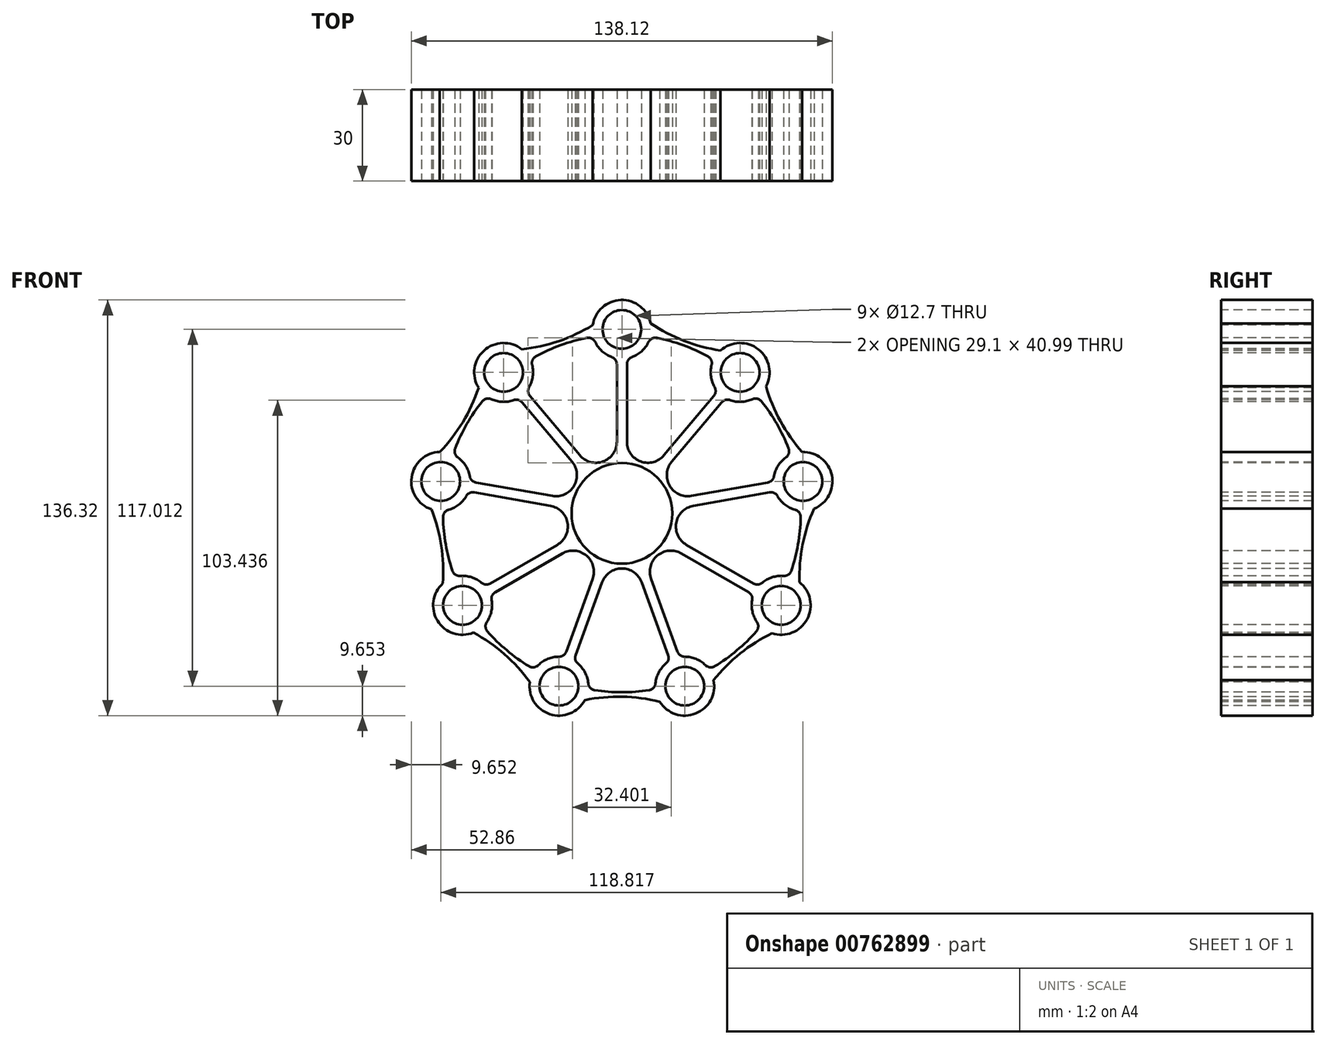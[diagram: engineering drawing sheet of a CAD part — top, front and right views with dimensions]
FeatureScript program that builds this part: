
annotation { "Feature Type Name" : "Feature", "Feature Type Description" : "" }
export const myFeature = defineFeature(function(context is Context, id is Id, definition is map)
    precondition{}
    {
        {
            var Q0;
            Q0=qCreatedBy(makeId("Front.planeOp"),FACE);
            var sketch = newSketch(context, id + "F0", { "sketchPlane" : qUnion([Q0])});
            skCircle(sketch, "E0", {"center": v(0, 0) * mm, "radius": 16.51 * mm});
            skCircle(sketch, "E1", {"center": v(0, 60.33) * mm, "radius": 6.35 * mm});
            skCircle(sketch, "E2.1.0", {"center": v(-38.78, 46.21) * mm, "radius": 6.35 * mm});
            skCircle(sketch, "E2.2.0", {"center": v(-59.4, 10.48) * mm, "radius": 6.35 * mm});
            skCircle(sketch, "E2.3.0", {"center": v(-52.24, -30.16) * mm, "radius": 6.35 * mm});
            skCircle(sketch, "E2.4.0", {"center": v(-20.63, -56.69) * mm, "radius": 6.35 * mm});
            skCircle(sketch, "E2.5.0", {"center": v(20.63, -56.69) * mm, "radius": 6.35 * mm});
            skCircle(sketch, "E2.6.0", {"center": v(52.24, -30.16) * mm, "radius": 6.35 * mm});
            skCircle(sketch, "E2.7.0", {"center": v(59.4, 10.48) * mm, "radius": 6.35 * mm});
            skCircle(sketch, "E2.8.0", {"center": v(38.78, 46.21) * mm, "radius": 6.35 * mm});
            skArc(sketch, "E3", {"start": v(-45.76, 36.72) * mm, "mid": v(-50.81, 29.34) * mm, "end": v(-54.68, 21.27) * mm});
            skArc(sketch, "E4", {"start": v(-8.71, 56.17) * mm, "mid": v(-6.49, 53.18) * mm, "end": v(-3.3, 51.25) * mm});
            skArc(sketch, "E5.1.0", {"start": v(-32.81, 53.8) * mm, "mid": v(-45.2, 53.41) * mm, "end": v(-47, 41.14) * mm});
            skArc(sketch, "E5.2.0", {"start": v(-56.83, 1.17) * mm, "mid": v(-53.5, 2.85) * mm, "end": v(-51.05, 5.65) * mm});
            skArc(sketch, "E5.3.0", {"start": v(-44.29, -35.63) * mm, "mid": v(-42.81, -32.2) * mm, "end": v(-42.74, -28.48) * mm});
            skArc(sketch, "E5.4.0", {"start": v(-11.02, -55.76) * mm, "mid": v(-12.1, -52.2) * mm, "end": v(-14.43, -49.3) * mm});
            skArc(sketch, "E5.5.0", {"start": v(12.43, -61.78) * mm, "mid": v(24.21, -65.65) * mm, "end": v(30.08, -54.74) * mm});
            skArc(sketch, "E5.6.0", {"start": v(49.24, -39.33) * mm, "mid": v(60.75, -34.73) * mm, "end": v(58.23, -22.6) * mm});
            skArc(sketch, "E5.7.0", {"start": v(53.8, 18.33) * mm, "mid": v(51.24, 15.62) * mm, "end": v(49.9, 12.15) * mm});
            skArc(sketch, "E5.8.0", {"start": v(29.43, 48.63) * mm, "mid": v(29.21, 44.9) * mm, "end": v(30.42, 41.38) * mm});
            skArc(sketch, "E6", {"start": v(-59.72, 20.12) * mm, "mid": v(-52.18, 29.92) * mm, "end": v(-47, 41.14) * mm});
            skArc(sketch, "E7.1.0", {"start": v(-58.68, -22.97) * mm, "mid": v(-59.2, -10.62) * mm, "end": v(-62.44, 1.31) * mm});
            skArc(sketch, "E7.2.0", {"start": v(-30.19, -55.32) * mm, "mid": v(-38.53, -46.2) * mm, "end": v(-48.68, -39.13) * mm});
            skArc(sketch, "E7.3.0", {"start": v(12.43, -61.78) * mm, "mid": v(0.18, -60.15) * mm, "end": v(-12.14, -61.27) * mm});
            skArc(sketch, "E7.4.0", {"start": v(49.24, -39.33) * mm, "mid": v(38.8, -45.96) * mm, "end": v(30.08, -54.74) * mm});
            skArc(sketch, "E7.5.0", {"start": v(63, 1.52) * mm, "mid": v(59.27, -10.27) * mm, "end": v(58.23, -22.6) * mm});
            skArc(sketch, "E7.6.0", {"start": v(47.29, 41.66) * mm, "mid": v(52, 30.23) * mm, "end": v(59.13, 20.12) * mm});
            skArc(sketch, "E7.7.0", {"start": v(9.45, 62.3) * mm, "mid": v(20.4, 56.58) * mm, "end": v(32.36, 53.42) * mm});
            skArc(sketch, "E7.8.0", {"start": v(-32.81, 53.8) * mm, "mid": v(-20.74, 56.46) * mm, "end": v(-9.55, 61.72) * mm});
            skArc(sketch, "E8.trimOffspring", {"start": v(9.45, 62.3) * mm, "mid": v(-0.3, 69.97) * mm, "end": v(-9.55, 61.72) * mm});
            skArc(sketch, "E9.trimOffspring", {"start": v(47.29, 41.66) * mm, "mid": v(44.75, 53.8) * mm, "end": v(32.36, 53.42) * mm});
            skArc(sketch, "E10.trimOffspring", {"start": v(63, 1.52) * mm, "mid": v(68.86, 12.44) * mm, "end": v(59.13, 20.12) * mm});
            skArc(sketch, "E11.trimOffspring", {"start": v(53, -20.54) * mm, "mid": v(49.3, -20.97) * mm, "end": v(46.04, -22.77) * mm});
            skArc(sketch, "E12.trimOffspring", {"start": v(27.4, -49.8) * mm, "mid": v(24.28, -47.75) * mm, "end": v(20.63, -47.03) * mm});
            skArc(sketch, "E13.trimOffspring", {"start": v(-30.19, -55.32) * mm, "mid": v(-23.65, -65.85) * mm, "end": v(-12.14, -61.27) * mm});
            skArc(sketch, "E14.trimOffspring", {"start": v(-58.68, -22.97) * mm, "mid": v(-60.45, -35.24) * mm, "end": v(-48.68, -39.13) * mm});
            skArc(sketch, "E15.trimOffspring", {"start": v(-59.72, 20.12) * mm, "mid": v(-68.96, 11.86) * mm, "end": v(-62.44, 1.31) * mm});
            skArc(sketch, "E16.trimOffspring", {"start": v(-42.78, 37.43) * mm, "mid": v(-39.15, 36.57) * mm, "end": v(-35.47, 37.14) * mm});
            skArc(sketch, "E17.trimOffspring", {"start": v(30.45, -50.16) * mm, "mid": v(37.71, -44.95) * mm, "end": v(44.1, -38.7) * mm});
            skArc(sketch, "E18.trimOffspring", {"start": v(-8.92, -58) * mm, "mid": v(0, -58.67) * mm, "end": v(8.92, -58) * mm});
            skArc(sketch, "E19.trimOffspring", {"start": v(55.56, -18.85) * mm, "mid": v(57.78, -10.19) * mm, "end": v(58.66, -1.29) * mm});
            skArc(sketch, "E20.trimOffspring", {"start": v(54.68, 21.27) * mm, "mid": v(50.81, 29.34) * mm, "end": v(45.76, 36.72) * mm});
            skArc(sketch, "E21.trimOffspring", {"start": v(28.21, 51.45) * mm, "mid": v(20.07, 55.14) * mm, "end": v(11.46, 57.54) * mm});
            skArc(sketch, "E22.trimOffspring", {"start": v(-11.46, 57.54) * mm, "mid": v(-20.07, 55.14) * mm, "end": v(-28.21, 51.45) * mm});
            skArc(sketch, "E23.trimOffspring", {"start": v(-58.66, -1.29) * mm, "mid": v(-57.78, -10.19) * mm, "end": v(-55.56, -18.85) * mm});
            skArc(sketch, "E24.trimOffspring", {"start": v(-44.1, -38.7) * mm, "mid": v(-37.71, -44.95) * mm, "end": v(-30.45, -50.16) * mm});
            skArc(sketch, "E25.trimOffspring", {"start": v(3.3, 51.25) * mm, "mid": v(6.49, 53.18) * mm, "end": v(8.71, 56.17) * mm});
            skArc(sketch, "E26.trimOffspring", {"start": v(35.47, 37.14) * mm, "mid": v(39.15, 36.57) * mm, "end": v(42.78, 37.43) * mm});
            skArc(sketch, "E27.trimOffspring", {"start": v(51.05, 5.65) * mm, "mid": v(53.5, 2.85) * mm, "end": v(56.83, 1.17) * mm});
            skArc(sketch, "E28.trimOffspring", {"start": v(42.74, -28.48) * mm, "mid": v(42.81, -32.2) * mm, "end": v(44.29, -35.63) * mm});
            skArc(sketch, "E29.trimOffspring", {"start": v(-30.42, 41.38) * mm, "mid": v(-29.21, 44.9) * mm, "end": v(-29.43, 48.63) * mm});
            skArc(sketch, "E30.trimOffspring", {"start": v(-49.9, 12.15) * mm, "mid": v(-51.24, 15.62) * mm, "end": v(-53.8, 18.33) * mm});
            skArc(sketch, "E31.trimOffspring", {"start": v(-46.04, -22.77) * mm, "mid": v(-49.3, -20.97) * mm, "end": v(-53, -20.54) * mm});
            skArc(sketch, "E32.trimOffspring", {"start": v(-20.63, -47.03) * mm, "mid": v(-24.28, -47.75) * mm, "end": v(-27.4, -49.8) * mm});
            skArc(sketch, "E33.trimOffspring", {"start": v(14.43, -49.3) * mm, "mid": v(12.1, -52.2) * mm, "end": v(11.02, -55.76) * mm});
            skLineSegment(sketch, "E34.trimOffspring", {"start": v(-13.84, 19.06) * mm, "end": v(-30.17, 38.52) * mm});
            skLineSegment(sketch, "E35.trimOffspring", {"start": v(-16.37, 16.93) * mm, "end": v(-32.7, 36.4) * mm});
            skLineSegment(sketch, "E36.trimOffspring", {"start": v(-22.85, 5.7) * mm, "end": v(-47.87, 10.12) * mm});
            skLineSegment(sketch, "E37.trimOffspring", {"start": v(-23.42, 2.45) * mm, "end": v(-48.45, 6.87) * mm});
            skLineSegment(sketch, "E38.trimOffspring", {"start": v(-21.17, -10.32) * mm, "end": v(-43.18, -23.02) * mm});
            skLineSegment(sketch, "E39.trimOffspring", {"start": v(-19.52, -13.18) * mm, "end": v(-41.53, -25.88) * mm});
            skLineSegment(sketch, "E40.trimOffspring", {"start": v(9.59, -21.51) * mm, "end": v(18.28, -45.4) * mm});
            skLineSegment(sketch, "E41.trimOffspring", {"start": v(6.48, -22.64) * mm, "end": v(15.17, -46.52) * mm});
            skLineSegment(sketch, "E42.trimOffspring", {"start": v(-6.48, -22.64) * mm, "end": v(-15.17, -46.52) * mm});
            skLineSegment(sketch, "E43.trimOffspring", {"start": v(-9.59, -21.51) * mm, "end": v(-18.28, -45.4) * mm});
            skLineSegment(sketch, "E44.trimOffspring", {"start": v(21.17, -10.32) * mm, "end": v(43.18, -23.02) * mm});
            skLineSegment(sketch, "E45.trimOffspring", {"start": v(19.52, -13.18) * mm, "end": v(41.53, -25.88) * mm});
            skLineSegment(sketch, "E46.trimOffspring", {"start": v(23.42, 2.45) * mm, "end": v(48.45, 6.87) * mm});
            skLineSegment(sketch, "E47.trimOffspring", {"start": v(22.85, 5.7) * mm, "end": v(47.87, 10.12) * mm});
            skLineSegment(sketch, "E48.trimOffspring", {"start": v(16.37, 16.93) * mm, "end": v(32.7, 36.4) * mm});
            skLineSegment(sketch, "E49.trimOffspring", {"start": v(13.84, 19.06) * mm, "end": v(30.17, 38.52) * mm});
            skLineSegment(sketch, "E50.trimOffspring", {"start": v(1.65, 23.5) * mm, "end": v(1.65, 48.9) * mm});
            skLineSegment(sketch, "E51.trimOffspring", {"start": v(-1.65, 23.5) * mm, "end": v(-1.65, 48.9) * mm});
            skArc(sketch, "E52", {"start": v(1.65, 23.5) * mm, "mid": v(6.2, 17) * mm, "end": v(13.84, 19.06) * mm});
            skArc(sketch, "E53.1.0", {"start": v(-13.84, 19.06) * mm, "mid": v(-6.2, 17) * mm, "end": v(-1.65, 23.5) * mm});
            skArc(sketch, "E53.2.0", {"start": v(-22.85, 5.7) * mm, "mid": v(-15.68, 9.05) * mm, "end": v(-16.37, 16.93) * mm});
            skArc(sketch, "E53.3.0", {"start": v(-21.17, -10.32) * mm, "mid": v(-17.83, -3.14) * mm, "end": v(-23.42, 2.45) * mm});
            skArc(sketch, "E53.4.0", {"start": v(-9.59, -21.51) * mm, "mid": v(-11.63, -13.87) * mm, "end": v(-19.52, -13.18) * mm});
            skArc(sketch, "E53.5.0", {"start": v(6.48, -22.64) * mm, "mid": v(0, -18.1) * mm, "end": v(-6.48, -22.64) * mm});
            skArc(sketch, "E53.6.0", {"start": v(19.52, -13.18) * mm, "mid": v(11.63, -13.87) * mm, "end": v(9.59, -21.51) * mm});
            skArc(sketch, "E53.7.0", {"start": v(23.42, 2.45) * mm, "mid": v(17.83, -3.14) * mm, "end": v(21.17, -10.32) * mm});
            skArc(sketch, "E53.8.0", {"start": v(16.37, 16.93) * mm, "mid": v(15.68, 9.05) * mm, "end": v(22.85, 5.7) * mm});
            skPoint(sketch, "E54.visualSharp", {"position": v(-30.07, 50.38) * mm});
            skArc(sketch, "E54.filletArc", {"start": v(-28.21, 51.45) * mm, "mid": v(-29.3, 50.25) * mm, "end": v(-29.43, 48.63) * mm});
            skPoint(sketch, "E55.visualSharp", {"position": v(-9.35, 57.92) * mm});
            skArc(sketch, "E55.filletArc", {"start": v(-8.71, 56.17) * mm, "mid": v(-9.85, 57.33) * mm, "end": v(-11.46, 57.54) * mm});
            skPoint(sketch, "E56.visualSharp", {"position": v(9.35, 57.92) * mm});
            skArc(sketch, "E56.filletArc", {"start": v(11.46, 57.54) * mm, "mid": v(9.85, 57.33) * mm, "end": v(8.71, 56.17) * mm});
            skPoint(sketch, "E57.visualSharp", {"position": v(30.07, 50.38) * mm});
            skArc(sketch, "E57.filletArc", {"start": v(29.43, 48.63) * mm, "mid": v(29.3, 50.25) * mm, "end": v(28.21, 51.45) * mm});
            skPoint(sketch, "E58.visualSharp", {"position": v(33.93, 37.87) * mm});
            skArc(sketch, "E58.filletArc", {"start": v(35.47, 37.14) * mm, "mid": v(33.97, 37.2) * mm, "end": v(32.7, 36.4) * mm});
            skPoint(sketch, "E59.visualSharp", {"position": v(44.4, 38.36) * mm});
            skArc(sketch, "E59.filletArc", {"start": v(45.76, 36.72) * mm, "mid": v(44.4, 37.59) * mm, "end": v(42.78, 37.43) * mm});
            skPoint(sketch, "E60.visualSharp", {"position": v(55.42, 19.27) * mm});
            skArc(sketch, "E60.filletArc", {"start": v(53.8, 18.33) * mm, "mid": v(54.75, 19.65) * mm, "end": v(54.68, 21.27) * mm});
            skPoint(sketch, "E61.visualSharp", {"position": v(58.67, 0.85) * mm});
            skArc(sketch, "E61.filletArc", {"start": v(58.66, -1.29) * mm, "mid": v(58.17, 0.26) * mm, "end": v(56.83, 1.17) * mm});
            skPoint(sketch, "E62.visualSharp", {"position": v(-44.4, 38.36) * mm});
            skArc(sketch, "E62.filletArc", {"start": v(-42.78, 37.43) * mm, "mid": v(-44.4, 37.59) * mm, "end": v(-45.76, 36.72) * mm});
            skPoint(sketch, "E63.visualSharp", {"position": v(-55.42, 19.27) * mm});
            skArc(sketch, "E63.filletArc", {"start": v(-54.68, 21.27) * mm, "mid": v(-54.75, 19.65) * mm, "end": v(-53.8, 18.33) * mm});
            skPoint(sketch, "E64.visualSharp", {"position": v(-58.67, 0.85) * mm});
            skArc(sketch, "E64.filletArc", {"start": v(-56.83, 1.17) * mm, "mid": v(-58.17, 0.26) * mm, "end": v(-58.66, -1.29) * mm});
            skPoint(sketch, "E65.visualSharp", {"position": v(-54.84, -20.87) * mm});
            skArc(sketch, "E65.filletArc", {"start": v(-55.56, -18.85) * mm, "mid": v(-54.57, -20.14) * mm, "end": v(-53, -20.54) * mm});
            skPoint(sketch, "E66.visualSharp", {"position": v(-45.49, -37.06) * mm});
            skArc(sketch, "E66.filletArc", {"start": v(-44.29, -35.63) * mm, "mid": v(-44.72, -37.2) * mm, "end": v(-44.1, -38.7) * mm});
            skPoint(sketch, "E67.visualSharp", {"position": v(-28.6, -51.23) * mm});
            skArc(sketch, "E67.filletArc", {"start": v(-30.45, -50.16) * mm, "mid": v(-28.86, -50.5) * mm, "end": v(-27.4, -49.8) * mm});
            skPoint(sketch, "E68.visualSharp", {"position": v(-11.03, -57.63) * mm});
            skArc(sketch, "E68.filletArc", {"start": v(-11.02, -55.76) * mm, "mid": v(-10.35, -57.24) * mm, "end": v(-8.92, -58) * mm});
            skPoint(sketch, "E69.visualSharp", {"position": v(11.03, -57.63) * mm});
            skArc(sketch, "E69.filletArc", {"start": v(8.92, -58) * mm, "mid": v(10.35, -57.24) * mm, "end": v(11.02, -55.76) * mm});
            skPoint(sketch, "E70.visualSharp", {"position": v(28.6, -51.23) * mm});
            skArc(sketch, "E70.filletArc", {"start": v(27.4, -49.8) * mm, "mid": v(28.86, -50.5) * mm, "end": v(30.45, -50.16) * mm});
            skPoint(sketch, "E71.visualSharp", {"position": v(45.49, -37.06) * mm});
            skArc(sketch, "E71.filletArc", {"start": v(44.1, -38.7) * mm, "mid": v(44.72, -37.2) * mm, "end": v(44.29, -35.63) * mm});
            skPoint(sketch, "E72.visualSharp", {"position": v(54.84, -20.87) * mm});
            skArc(sketch, "E72.filletArc", {"start": v(53, -20.54) * mm, "mid": v(54.57, -20.14) * mm, "end": v(55.56, -18.85) * mm});
            skPoint(sketch, "E73.visualSharp", {"position": v(-49.76, 10.45) * mm});
            skArc(sketch, "E73.filletArc", {"start": v(-49.9, 12.15) * mm, "mid": v(-49.2, 10.81) * mm, "end": v(-47.87, 10.12) * mm});
            skPoint(sketch, "E74.visualSharp", {"position": v(-50.33, 7.2) * mm});
            skArc(sketch, "E74.filletArc", {"start": v(-48.45, 6.87) * mm, "mid": v(-49.94, 6.67) * mm, "end": v(-51.05, 5.65) * mm});
            skPoint(sketch, "E75.visualSharp", {"position": v(-44.83, -23.98) * mm});
            skArc(sketch, "E75.filletArc", {"start": v(-46.04, -22.77) * mm, "mid": v(-44.65, -23.35) * mm, "end": v(-43.18, -23.02) * mm});
            skPoint(sketch, "E76.visualSharp", {"position": v(-43.18, -26.84) * mm});
            skArc(sketch, "E76.filletArc", {"start": v(-41.53, -25.88) * mm, "mid": v(-42.54, -27) * mm, "end": v(-42.74, -28.48) * mm});
            skPoint(sketch, "E77.visualSharp", {"position": v(-18.93, -47.19) * mm});
            skArc(sketch, "E77.filletArc", {"start": v(-20.63, -47.03) * mm, "mid": v(-19.2, -46.58) * mm, "end": v(-18.28, -45.4) * mm});
            skPoint(sketch, "E78.visualSharp", {"position": v(-15.83, -48.32) * mm});
            skArc(sketch, "E78.filletArc", {"start": v(-15.17, -46.52) * mm, "mid": v(-15.24, -48.02) * mm, "end": v(-14.43, -49.3) * mm});
            skPoint(sketch, "E79.visualSharp", {"position": v(15.83, -48.32) * mm});
            skArc(sketch, "E79.filletArc", {"start": v(14.43, -49.3) * mm, "mid": v(15.24, -48.02) * mm, "end": v(15.17, -46.52) * mm});
            skPoint(sketch, "E80.visualSharp", {"position": v(18.93, -47.19) * mm});
            skArc(sketch, "E80.filletArc", {"start": v(18.28, -45.4) * mm, "mid": v(19.2, -46.58) * mm, "end": v(20.63, -47.03) * mm});
            skPoint(sketch, "E81.visualSharp", {"position": v(43.18, -26.84) * mm});
            skArc(sketch, "E81.filletArc", {"start": v(42.74, -28.48) * mm, "mid": v(42.54, -27) * mm, "end": v(41.53, -25.88) * mm});
            skPoint(sketch, "E82.visualSharp", {"position": v(44.83, -23.98) * mm});
            skArc(sketch, "E82.filletArc", {"start": v(43.18, -23.02) * mm, "mid": v(44.65, -23.35) * mm, "end": v(46.04, -22.77) * mm});
            skPoint(sketch, "E83.visualSharp", {"position": v(50.33, 7.2) * mm});
            skArc(sketch, "E83.filletArc", {"start": v(51.05, 5.65) * mm, "mid": v(49.94, 6.67) * mm, "end": v(48.45, 6.87) * mm});
            skPoint(sketch, "E84.visualSharp", {"position": v(49.76, 10.45) * mm});
            skArc(sketch, "E84.filletArc", {"start": v(47.87, 10.12) * mm, "mid": v(49.2, 10.81) * mm, "end": v(49.9, 12.15) * mm});
            skPoint(sketch, "E85.visualSharp", {"position": v(31.4, 39.99) * mm});
            skArc(sketch, "E85.filletArc", {"start": v(30.17, 38.52) * mm, "mid": v(30.75, 39.91) * mm, "end": v(30.42, 41.38) * mm});
            skPoint(sketch, "E86.visualSharp", {"position": v(1.65, 50.82) * mm});
            skArc(sketch, "E86.filletArc", {"start": v(3.3, 51.25) * mm, "mid": v(2.1, 50.34) * mm, "end": v(1.65, 48.9) * mm});
            skPoint(sketch, "E87.visualSharp", {"position": v(-1.65, 50.82) * mm});
            skArc(sketch, "E87.filletArc", {"start": v(-1.65, 48.9) * mm, "mid": v(-2.1, 50.34) * mm, "end": v(-3.3, 51.25) * mm});
            skPoint(sketch, "E88.visualSharp", {"position": v(-31.4, 39.99) * mm});
            skArc(sketch, "E88.filletArc", {"start": v(-30.42, 41.38) * mm, "mid": v(-30.75, 39.91) * mm, "end": v(-30.17, 38.52) * mm});
            skPoint(sketch, "E89.visualSharp", {"position": v(-33.93, 37.87) * mm});
            skArc(sketch, "E89.filletArc", {"start": v(-32.7, 36.4) * mm, "mid": v(-33.97, 37.2) * mm, "end": v(-35.47, 37.14) * mm});
            skSolve(sketch);
        }
        {
            var Q0;
            Q0=makeQuery(id+"F0.imprint","IMPRINT",FACE,{"disambiguationData":[TD([[makeQuery(id+"F0.imprint","IMPRINT",EDGE,{"derivedFrom":sQuery(id+"F0.wireOp",EDGE,"E0")}),-1.0]])]});
            extrude(context, id + "F1", {"entities" : qUnion([Q0]), "oppositeDirection" : true, "depth" : 30 * mm, "offsetDistance" : 25 * mm});
        }
    });
